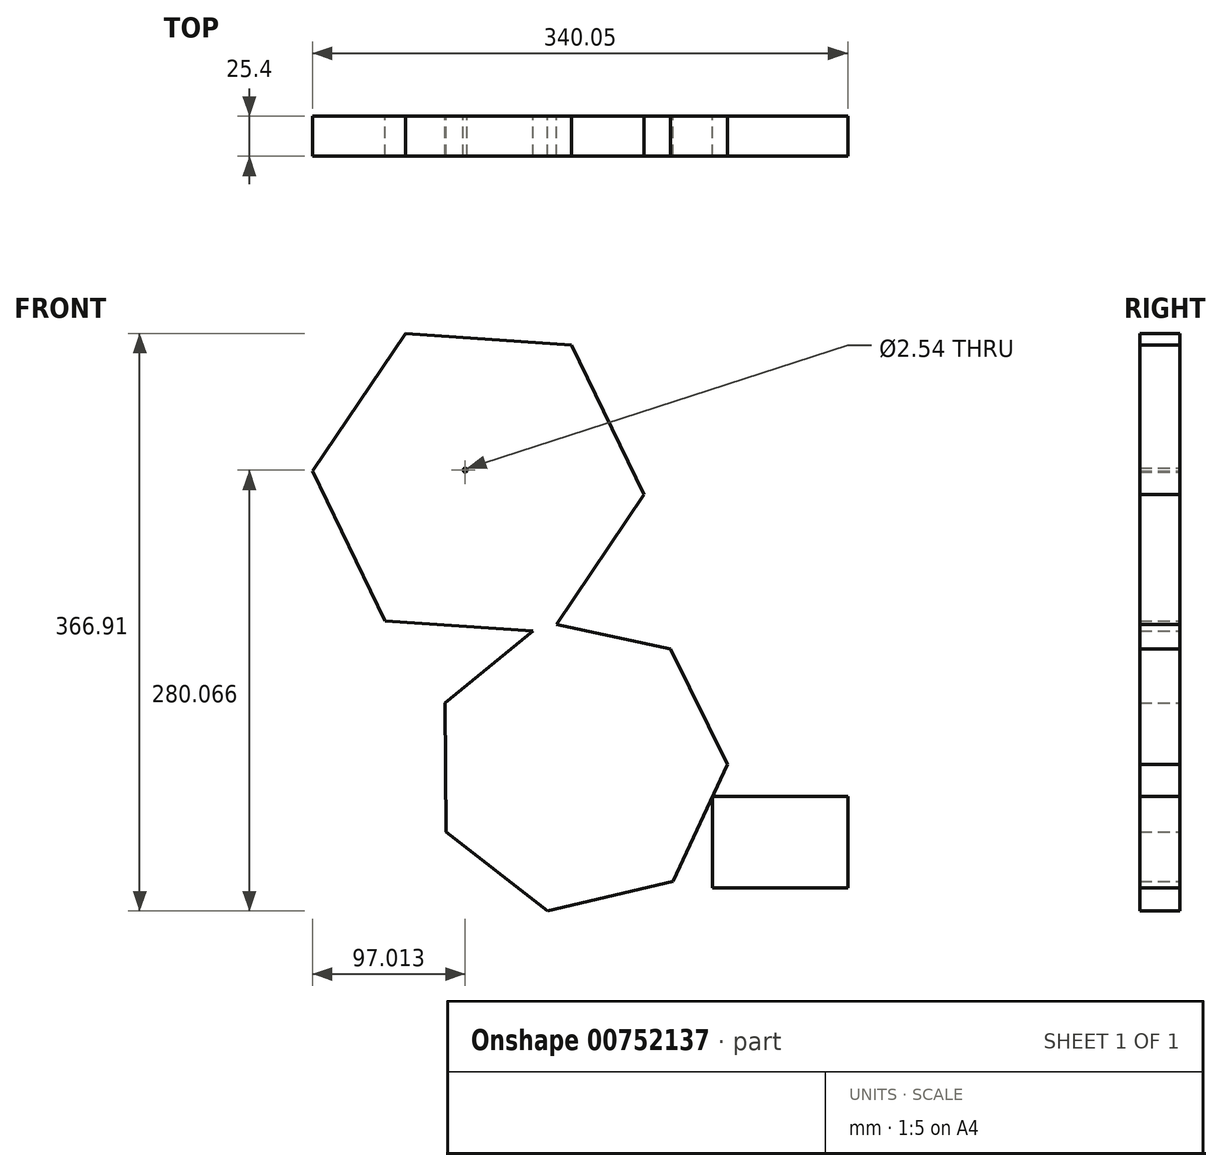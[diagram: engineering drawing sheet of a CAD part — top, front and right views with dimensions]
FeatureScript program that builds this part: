
annotation { "Feature Type Name" : "Feature", "Feature Type Description" : "" }
export const myFeature = defineFeature(function(context is Context, id is Id, definition is map)
    precondition{}
    {
        {
            var Q0;
            Q0=qCreatedBy(makeId("Front.planeOp"),FACE);
            var sketch = newSketch(context, id + "F0", { "sketchPlane" : qUnion([Q0])});
            skCircle(sketch, "E0.cCircle", {"center": v(-102.29, 57.05) * mm, "radius": 84.92 * mm, "construction": true});
            skLineSegment(sketch, "E0.0", {"start": v(-187.62, 97.1) * mm, "end": v(-124.18, 148.73) * mm});
            skLineSegment(sketch, "E0.1", {"start": v(-124.18, 148.73) * mm, "end": v(-44.26, 131.33) * mm});
            skLineSegment(sketch, "E0.2", {"start": v(-44.26, 131.33) * mm, "end": v(-8.03, 58) * mm});
            skLineSegment(sketch, "E0.3", {"start": v(-8.03, 58) * mm, "end": v(-42.78, -16.05) * mm});
            skLineSegment(sketch, "E0.4", {"start": v(-42.78, -16.05) * mm, "end": v(-122.34, -35.05) * mm});
            skLineSegment(sketch, "E0.5", {"start": v(-122.34, -35.05) * mm, "end": v(-186.8, 15.3) * mm});
            skLineSegment(sketch, "E0.6", {"start": v(-186.8, 15.3) * mm, "end": v(-187.62, 97.1) * mm});
            skPoint(sketch, "E0.0.midPoint", {"position": v(-155.9, 122.91) * mm});
            skCircle(sketch, "E1.cCircle", {"center": v(-166.42, 236.92) * mm, "radius": 91.47 * mm, "construction": true});
            skLineSegment(sketch, "E1.0", {"start": v(-271.78, 244.32) * mm, "end": v(-212.69, 331.86) * mm});
            skLineSegment(sketch, "E1.1", {"start": v(-212.69, 331.86) * mm, "end": v(-107.33, 324.46) * mm});
            skLineSegment(sketch, "E1.2", {"start": v(-107.33, 324.46) * mm, "end": v(-61.06, 229.52) * mm});
            skLineSegment(sketch, "E1.3", {"start": v(-61.06, 229.52) * mm, "end": v(-120.15, 141.98) * mm});
            skLineSegment(sketch, "E1.4", {"start": v(-120.15, 141.98) * mm, "end": v(-225.51, 149.38) * mm});
            skLineSegment(sketch, "E1.5", {"start": v(-225.51, 149.38) * mm, "end": v(-271.78, 244.32) * mm});
            skPoint(sketch, "E1.0.midPoint", {"position": v(-242.23, 288.1) * mm});
            skLineSegment(sketch, "E2.bottom", {"start": v(-17.54, 37.74) * mm, "end": v(68.27, 37.74) * mm});
            skLineSegment(sketch, "E2.top", {"start": v(-17.54, -20.35) * mm, "end": v(68.27, -20.35) * mm});
            skLineSegment(sketch, "E2.left", {"start": v(-17.54, 37.74) * mm, "end": v(-17.54, -20.35) * mm});
            skLineSegment(sketch, "E2.right", {"start": v(68.27, 37.74) * mm, "end": v(68.27, -20.35) * mm});
            skSolve(sketch);
        }
        {
            var Q0;
            Q0 = qSketchRegion(id + "F0", true);
            extrude(context, id + "F1", {"entities" : qUnion([Q0]), "depth" : 25.4 * mm, "offsetDistance" : 25.4 * mm});
        }
        {
            var Q0;
            Q0=makeQuery(id+"F1.opExtrude","CAP_FACE",FACE,{"disambiguationData":[OSD([sQuery(id+"F0.wireOp",EDGE,"E0.0"),sQuery(id+"F0.wireOp",EDGE,"E0.1"),sQuery(id+"F0.wireOp",EDGE,"E0.2"),sQuery(id+"F0.wireOp",EDGE,"E0.3"),sQuery(id+"F0.wireOp",EDGE,"E0.4"),sQuery(id+"F0.wireOp",EDGE,"E0.5"),sQuery(id+"F0.wireOp",EDGE,"E0.6"),sQuery(id+"F0.wireOp",EDGE,"E1.0"),sQuery(id+"F0.wireOp",EDGE,"E1.1"),sQuery(id+"F0.wireOp",EDGE,"E1.2"),sQuery(id+"F0.wireOp",EDGE,"E1.3"),sQuery(id+"F0.wireOp",EDGE,"E1.4"),sQuery(id+"F0.wireOp",EDGE,"E1.5")])],"isStart":true});
            var sketch = newSketch(context, id + "F2", { "sketchPlane" : qUnion([Q0])});
            skPoint(sketch, "E3", {"position": v(174.77, 245.02) * mm});
            skPoint(sketch, "E4", {"position": v(97.2, 47.45) * mm});
            skPoint(sketch, "E5", {"position": v(-26.02, 0) * mm});
            skSolve(sketch);
        }
        {
            var Q0;
            Q0=sQuery(id+"F2.wireOp",VERTEX,"E3");
            var Q1;
            Q1=makeQuery(id+"F1.opExtrude","SWEPT_BODY",BODY,{"disambiguationData":[OSD([sQuery(id+"F0.wireOp",EDGE,"E0.0"),sQuery(id+"F0.wireOp",EDGE,"E0.1"),sQuery(id+"F0.wireOp",EDGE,"E0.2"),sQuery(id+"F0.wireOp",EDGE,"E0.3"),sQuery(id+"F0.wireOp",EDGE,"E0.4"),sQuery(id+"F0.wireOp",EDGE,"E0.5"),sQuery(id+"F0.wireOp",EDGE,"E0.6"),sQuery(id+"F0.wireOp",EDGE,"E1.0"),sQuery(id+"F0.wireOp",EDGE,"E1.1"),sQuery(id+"F0.wireOp",EDGE,"E1.2"),sQuery(id+"F0.wireOp",EDGE,"E1.3"),sQuery(id+"F0.wireOp",EDGE,"E1.4"),sQuery(id+"F0.wireOp",EDGE,"E1.5")])]});
            hole(context, id + "F3", {"style" : HoleStyle.SIMPLE, "endStyle" : HoleEndStyle.THROUGH, "holeDiameter" : 2.54 * mm, "majorDiameter" : 6.35 * mm, "isTappedThrough" : true, "tappedDepth" : 12.7 * mm, "tapClearance" : 3, "locations" : qUnion([Q0]), "scope" : qUnion([Q1])});
        }
    });
